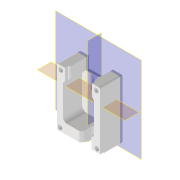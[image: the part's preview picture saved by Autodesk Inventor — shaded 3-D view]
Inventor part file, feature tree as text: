
AUTODESK INVENTOR PART (.ipt)
format: ipt  version: 2022 (Build 260153000, 153)  size: 456,704 bytes
history: native  units: mm
features: reference x19, other x12, sketch x11, extrude x10, projected_geometry x8, plane x5, fillet x2, hole x2, chamfer x1
ambient origin geometry x8: Origin, YZ Plane, XZ Plane, XY Plane, X Axis, Y Axis, Z Axis, Center Point
bodies: Solid1 (feature_tree)
feature tree (70):
  plane  "Work Plane1"
  extrude  "Extrusion1"  Depth=53.8mm
  extrude  "IM_offset"  Depth=53.8mm
  plane  "Arbeitsebene5"
  plane  "Arbeitsebene6"
  extrude  "Extrusion26"  Depth=45.0mm
  chamfer  "Fase2"  Distance=0.1mm
  plane  "Arbeitsebene9"
  extrude  "Extrusion29"  Depth=10.0mm
  extrude  "Extrusion30"  Depth=10.0mm
  plane  "Arbeitsebene10"
  extrude  "Extrusion31"  Depth=10.0mm TaperAngle=0.0deg
  fillet  "Rundung3"  Radius=7.5mm
  hole  "Bohrung2"  [1 undecoded]
  extrude  "Extrusion32"  Depth=2.0mm TaperAngle=45.0deg
  hole  "Bohrung3"  [1 undecoded]
  extrude  "Extrusion33"  Depth=10.0mm
  extrude  "Extrusion34"  Depth=10.0mm
  fillet  "Rundung4"  [1 undecoded]
  extrude  "Extrusion35"  Depth=10.0mm TaperAngle=0.0deg
  sketch  "Sketch1"  dims[d10=12.0mm d11=0.0mm d18=53.8mm]
  reference  "Reference1"
  reference  "Reference2"
  reference  "Reference3"
  reference  "Reference4"
  reference  "Reference9"
  reference  "Reference20"
  reference  "Reference21"
  reference  "Reference22"
  reference  "Reference23"
  reference  "Reference24"
  sketch  "Skizze4"  dims[d19=45.0deg d20=53.8mm]
  projected_geometry  "Projizierte Kontur1"
  sketch  "Skizze31"  dims[d21=45.0mm d22=45.0mm]
  projected_geometry  "Projizierte Kontur17"
  sketch  "Skizze34"  dims[d30=20.0mm]
  reference  "Referenz35"
  sketch  "Skizze35"  dims[d31=20.0mm]
  reference  "Referenz36"
  reference  "Referenz37"
  reference  "Referenz38"
  reference  "Referenz39"
  reference  "Referenz40"
  sketch  "Skizze37"  dims[d32=2.8mm]
  projected_geometry  "Projizierte Kontur18"
  reference  "Referenz41"
  sketch  "Skizze38"  dims[d33=2.8mm]
  reference  "Referenz42"
  sketch  "Skizze39"  dims[d34=2.8mm]
  reference  "Referenz43"
  sketch  "Skizze40"  dims[d35=3.0mm]
  projected_geometry  "Projizierte Kontur19"
  sketch  "Skizze41"  dims[d36=0.1mm]
  projected_geometry  "Projizierte Kontur20"
  sketch  "Skizze42"  dims[d37=0.1mm d38=0.1mm d39=0.1mm d40=0.2mm d41=10.0mm d42=0.0mm d181=7.5mm d182=10.0mm d183=0.0mm d184=0.5mm d185=2.0mm d186=45.0deg d193=-1.5mm d194=8.6mm d195=8.6mm d196=0.0mm d197=0.0mm d198=10.0mm d199=0.0mm d200=4.0mm d201=12.0mm d202=0.0mm d203=1.0mm d204=30.0mm d205=30.0mm d206=2.8mm d207=6.0mm d208=8.0mm d209=6.0mm d210=90.0deg d211=8.0mm d212=20.594885mm d213=0.0mm d214=0.0mm d215=2.8mm d216=6.0mm d217=4.0mm d218=2.0mm d219=90.0deg d220=8.0mm d221=20.594885mm d222=2.0mm d223=0.0mm d224=1.0mm d225=5.0mm d226=8.0mm d227=10.0mm d228=0.0mm d229=2.0mm d230=10.0mm d231=0.0mm d160=0.5mm d161=0.872665mm d162=0.5mm d163=0.872665mm]
  projected_geometry  "Projizierte Kontur21"
  projected_geometry  "Projizierte Kontur22"
  projected_geometry  "Projizierte Kontur23"
  other  "Assembly_Cube_v2_Thorlabs.iam"
  other  "10_Cube_Base:1"
  other  "00_Base_v0:1"
  other  "Assembly_Cube_Kinematic_Mirrormount_v2.iam"
  other  "Assembly_Cube_empty_1x1_v2:1"
  other  "10_Cube_1x1_v2:1"
  other  "10_Lid_1x1_v2:1"
  other  "Assembly_Cube_SEEED_Xiao_Sense_Camera_v3.iam"
  other  "00_Seeeduino Xiao:1"
  other  "00_ESP3-CAM:1"
  other  "00_ESP32_XIAO_Adapter_lid:1"
  other  "10_Cube_Lid:1"
note: 3 required parameter values undecoded (feature->parameter linkage not recoverable at this tier; creation-order binding heuristic only, values carry confidence <= 0.55)
